# Revit family: Haworth_ImprovHE_Stool
name_source: partatom
category: Furniture
revit_build: Autodesk Revit 2018 (Build: 20170223_1515(x64)
units: mm (PartAtom-declared; Revit-internal decimal feet)

## family parameters
Always vertical = Yes
Cut with Voids When Loaded = No
OmniClass Number = 23.40.20.00
OmniClass Title = General Furniture and Specialties
Room Calculation Point = No
Shared = No
Work Plane-Based = No

## types (5) — shared parameters
Actual Depth = 2' - 1"
Actual Height = 3' - 8 1/2"
Actual Width = 2' - 1 1/2"
Arm Cap Finish = Haworth _ Polymer _ Black
Assembly Code = E2020200
Base Finish = Haworth _ Polymer _ Black
Caster Finish = Haworth _ Polymer _ Black
Depth = 25 in.
Description = Haworth - Chair - Improv HE - Stool
Height = 42 - 54 in.
Manufacturer = Haworth
Model = Haworth - Chair - Improv HE - Stool
Revision = 2
Seat Finish = Haworth _ Fabric _ Tellure _ Tomato 3A-43
Size = Verify Final Dim. w/ Haworth
Sustainability Info = http://www.haworth.com
URL = http://haworth.com
URL - Product = https://www.haworth.com
Warranty = http://www.haworth.com
Width = 25.5 in.

## per-type parameters (varying)
| type | 3D Arms |
| Height Adjustable Arms | No |
| 3D Arms | Yes |
| Fixed Arms | No |
| Flipper Arms | No |
| Without Arms | No |

type visibility flags (boolean, named after types; folded from table):
- Height Adjustable Arms: Yes: Height Adjustable Arms
- 3D Arms: Yes: (none)
- Fixed Arms: Yes: Fixed Arms
- Flipper Arms: Yes: Flipper Arms
- Without Arms: Yes: Without Arms

## geometry (parser evidence)
native form markers: Sweep x18
no freeform markers — native parametric forms only
